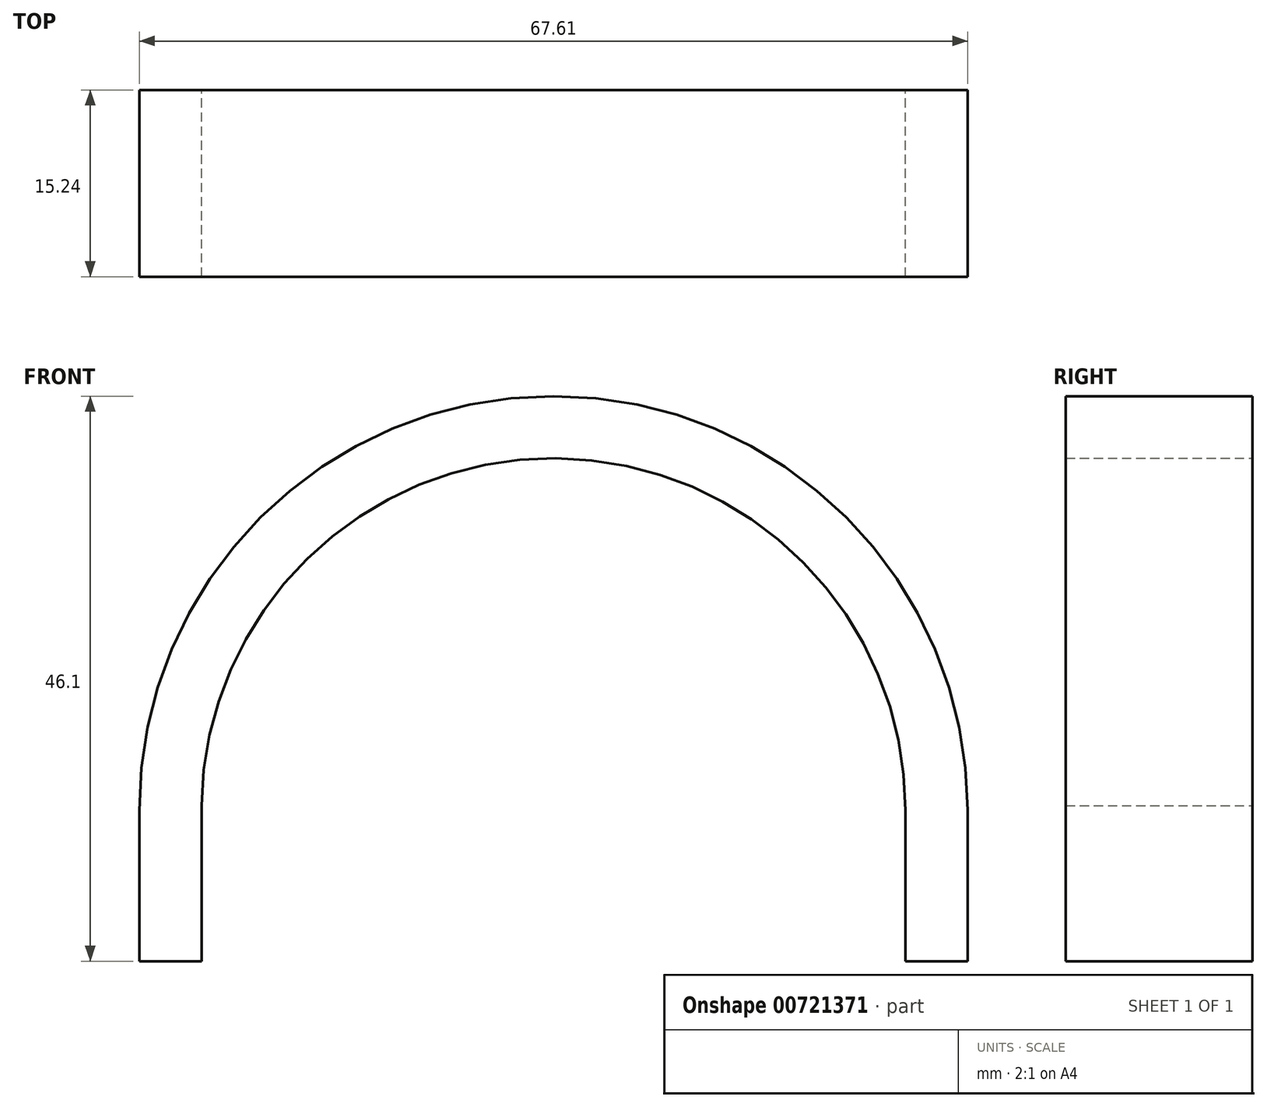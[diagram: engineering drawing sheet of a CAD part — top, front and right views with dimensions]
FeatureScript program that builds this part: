
annotation { "Feature Type Name" : "Feature", "Feature Type Description" : "" }
export const myFeature = defineFeature(function(context is Context, id is Id, definition is map)
    precondition{}
    {
        {
            var Q0;
            Q0=qCreatedBy(makeId("Front.planeOp"),FACE);
            var sketch = newSketch(context, id + "F0", { "sketchPlane" : qUnion([Q0])});
            skLineSegment(sketch, "E0", {"start": v(-35.87, 0) * mm, "end": v(-35.87, 12.3) * mm});
            skArc(sketch, "E1", {"start": v(31.74, 12.3) * mm, "mid": v(-2.07, 46.1) * mm, "end": v(-35.87, 12.3) * mm});
            skLineSegment(sketch, "E2", {"start": v(31.74, 12.3) * mm, "end": v(31.74, 0) * mm});
            skLineSegment(sketch, "E3", {"start": v(31.74, 0) * mm, "end": v(26.66, 0) * mm});
            skLineSegment(sketch, "E4", {"start": v(26.66, 0) * mm, "end": v(26.66, 12.3) * mm});
            skLineSegment(sketch, "E5", {"start": v(-35.87, 0) * mm, "end": v(-30.8, 0) * mm});
            skLineSegment(sketch, "E6", {"start": v(-30.8, 0) * mm, "end": v(-30.8, 12.7) * mm});
            skArc(sketch, "E7", {"start": v(26.66, 12.3) * mm, "mid": v(-1.87, 41.02) * mm, "end": v(-30.8, 12.7) * mm});
            skSolve(sketch);
        }
        {
            var Q0;
            Q0 = qSketchRegion(id + "F0", true);
            extrude(context, id + "F1", {"entities" : qUnion([Q0]), "depth" : 15.24 * mm, "offsetDistance" : 25.4 * mm});
        }
    });
